# Revit family: LAMP_FIL 45 1400MM OPAL SUSPENDED
name_source: partatom
category: Luminarias
revit_build: Autodesk Revit 2018 (Build: 20170223_1515(x64)
units: mm (PartAtom-declared; Revit-internal decimal feet)

## family parameters
Anfitrión = Cara
Compartido = No
Corte con vacíos al cargar = No
Cota de conector redondo = Diámetro de uso
Origen de luz = Sí
Punto de cálculo de habitación = No
Tipo de pieza = Normal

## types (24) — shared parameters
CRI = 80
Cambio de temperatura de color de luz atenuada = <Ninguno>
Dimensions = 1400x45x80
Elevación por defecto = 1219 mm
Fabricante = LAMP
Filtro de color = 16777215
Gear = Electronic
IEE = A+
Installation instructions = https://www.lamp.es
Insulation class = I
Lamp = MID-POWER LED
Last update = 15/03/2021
MacAdam = 3
Manufacturer URL = http://www.lamp.es
Manufacturer country = Spain
Manufacturer name = LAMP
Material difusor = LAMP_PC Difusor Opal Fil
Material suspension = LAMP_Acero genérico
Power Supply = 220-240V 50/60Hz
Product URL = https://www.lamp.es
Product datasheet = http://www.lamp.es
Protection rating = IP20 / IK07
Type = MID POWER TRIDONIC
Ángulo de inclinación = -90.00°

## per-type parameters (varying)
| type | Archivo de red fotométrica | Descripción | Efficacy | Finish | LED Lifetime | Longitud de línea de emisión | Material perfil | Modelo | Plum | Power | Product code | Weight |
| 3225LM 3000K DALI BLACK | F41SF140MOOP830nb.IES | FIL45 SUR 1400 3250 WW OPAL DALI BK. | 107 lm/W | Matte black RAL 9011 | 70.000 L80 B10 | 610 mm | LAMP_Aluminio Perfil Fil NG | F41SF140MOOP830DB | 20 W | 19 W | F41SF140MOOP830DB | 3.17 kg |
| 3225LM 3000K DALI GREY | F41SF140MOOP830nG.IES | FIL45 SUR 1400 3250 WW OPAL DALI GR. | 107 lm/W | Gloss grey | 70.000 L80 B10 | 610 mm | LAMP_Aluminio Perfil Fil GR | F41SF140MOOP830DG | 20 W | 19 W | F41SF140MOOP830DG | 3.17 kg |
| 3225LM 3000K DALI WHITE | F41SF140MOOP830nW.IES | FIL45 SUR 1400 3250 WW OPAL DALI WH. | 107 lm/W | Matte white RAL 9010 | 70.000 L80 B10 | 610 mm | LAMP_Aluminio Perfil Fil BL | F41SF140MOOP830DW | 20 W | 19 W | F41SF140MOOP830DW | 3.17 kg |
| 3225LM 3000K  BLACK | F41SF140MOOP830NB.IES | FIL45 SUR 1400 3250 WW OPAL BK. | 107 lm/W | Matte black RAL 9011 | 70.000 L80 B10 | 1400 mm  [stored 4.59318 ft] | LAMP_Aluminio Perfil Fil NG | F41SF140MOOP830NB | 20 W | 19 W | F41SF140MOOP830NB | 3.00 kg |
| 3225LM 3000K  GREY | F41SF140MOOP830NG.IES | FIL45 SUR 1400 3250 WW OPAL GR. | 107 lm/W | Gloss grey | 70.000 L80 B10 | 610 mm | LAMP_Aluminio Perfil Fil GR | F41SF140MOOP830NG | 20 W | 19 W | F41SF140MOOP830NG | 3.00 kg |
| 3225LM 3000K  WHITE | F41SF140MOOP830NW.IES | FIL45 SUR 1400 3250 WW OPAL WH. | 107 lm/W | Matte white RAL 9010 | 70.000 L80 B10 | 610 mm | LAMP_Aluminio Perfil Fil BL | F41SF140MOOP830NW | 20 W | 19 W | F41SF140MOOP830NW | 3.00 kg |
| 3225LM 4000K DALI BLACK | F41SF140MOOP840nB.IES | FIL45 SUR 1400 3250 NW OPAL DALI BK. | 117 lm/W | Matte black RAL 9011 | 70.000 L80 B10 | 610 mm | LAMP_Aluminio Perfil Fil NG | F41SF140MOOP840DB | 20 W | 19 W | F41SF140MOOP840DB | 3.17 kg |
| 3225LM 4000K DALI GREY | F41SF140MOOP840nG.IES | FIL45 SUR 1400 3250 NW OPAL DALI GR. | 117 lm/W | Gloss grey | 70.000 L80 B10 | 610 mm | LAMP_Aluminio Perfil Fil GR | F41SF140MOOP840DG | 20 W | 19 W | F41SF140MOOP840DG | 3.17 kg |
| 3225LM 4000K DALI WHITE | F41SF140MOOP840nW.IES | FIL45 SUR 1400 3250 NW OPAL DALI WH. | 117 lm/W | Matte white RAL 9010 | 70.000 L80 B10 | 610 mm | LAMP_Aluminio Perfil Fil BL | F41SF140MOOP840DW | 20 W | 19 W | F41SF140MOOP840DW | 3.17 kg |
| 3225LM 4000K  BLACK | F41SF140MOOP840NB.IES | FIL45 SUR 1400 3250 NW OPAL BK. | 117 lm/W | Matte black RAL 9011 | 70.000 L80 B10 | 610 mm | LAMP_Aluminio Perfil Fil NG | F41SF140MOOP840NB | 20 W | 19 W | F41SF140MOOP840NB | 3.00 kg |
| 3225LM 4000K  GREY | F41SF140MOOP840NG.IES | FIL45 SUR 1400 3250 NW OPAL GR. | 117 lm/W | Gloss grey | 70.000 L80 B10 | 610 mm | LAMP_Aluminio Perfil Fil GR | F41SF140MOOP840NG | 20 W | 19 W | F41SF140MOOP840NG | 3.00 kg |
| 3225LM 4000K  WHITE | F41SF140MOOP840NW.IES | FIL45 SUR 1400 3250 NW OPAL WH. | 117 lm/W | Matte white RAL 9010 | 70.000 L80 B10 | 610 mm | LAMP_Aluminio Perfil Fil BL | F41SF140MOOP840NW | 20 W | 19 W | F41SF140MOOP840NW | 3.00 kg |
| 7750LM 3000K DALI BLACK | F41SF140HOOP830nB.IES | FIL45 SUR 1400 7750 WW OPAL DALI BK. | 95 lm/W | Matte black RAL 9011 | 72.000 L80 B10 | 610 mm | LAMP_Aluminio Perfil Fil NG | F41SF140HOOP830DB | 49 W | 45 W | F41SF140HOOP830DB | 3.19 kg |
| 7750LM 3000K DALI GREY | F41SF140HOOP830nG.IES | FIL45 SUR 1400 7750 WW OPAL DALI GR. | 95 lm/W | Gloss grey | 72.000 L80 B10 | 610 mm | LAMP_Aluminio Perfil Fil GR | F41SF140HOOP830DG | 49 W | 45 W | F41SF140HOOP830DG | 3.19 kg |
| 7750LM 3000K DALI WHITE | F41SF140HOOP830nW.IES | FIL45 SUR 1400 7750 WW OPAL DALI WH. | 95 lm/W | Matte white RAL 9010 | 72.000 L80 B10 | 610 mm | LAMP_Aluminio Perfil Fil BL | F41SF140HOOP830DW | 49 W | 45 W | F41SF140HOOP830DW | 3.19 kg |
| 7750LM 3000K  BLACK | F41SF140HOOP830NB.IES | FIL45 SUR 1400 7750 WW OPAL BK. | 95 lm/W | Matte black RAL 9011 | 72.000 L80 B10 | 610 mm | LAMP_Aluminio Perfil Fil NG | F41SF140HOOP830NB | 49 W | 45 W | F41SF140HOOP830NB | 3.05 kg |
| 7750LM 3000K  GREY | F41SF140HOOP830NG.IES | FIL45 SUR 1400 7750 WW OPAL GR. | 95 lm/W | Gloss grey | 72.000 L80 B10 | 610 mm | LAMP_Aluminio Perfil Fil GR | F41SF140HOOP830NG | 49 W | 45 W | F41SF140HOOP830NG | 3.05 kg |
| 7750LM 3000K  WHITE | F41SF140HOOP830NW.IES | FIL45 SUR 1400 7750 WW OPAL WH. | 95 lm/W | Matte white RAL 9010 | 72.000 L80 B10 | 610 mm | LAMP_Aluminio Perfil Fil BL | F41SF140HOOP830NW | 49 W | 45 W | F41SF140HOOP830NW | 3.05 kg |
| 7750LM 4000K DALI BLACK | F41SF140HOOP840nB.IES | FIL45 SUR 1400 7750 NW OPAL DALI BK. | 95 lm/W | Matte black RAL 9011 | 72.000 L80 B10 | 610 mm | LAMP_Aluminio Perfil Fil NG | F41SF140HOOP840DB | 49 W | 45 W | F41SF140HOOP840DB | 3.19 kg |
| 7750LM 4000K DALI GREY | F41SF140HOOP840nG.IES | FIL45 SUR 1400 7750 NW OPAL DALI GR. | 95 lm/W | Gloss grey | 72.000 L80 B10 | 610 mm | LAMP_Aluminio Perfil Fil GR | F41SF140HOOP840DG | 49 W | 45 W | F41SF140HOOP840DG | 3.19 kg |
| 7750LM 4000K DALI WHITE | F41SF140HOOP840nW.IES | FIL45 SUR 1400 7750 NW OPAL DALI WH. | 95 lm/W | Matte white RAL 9010 | 72.000 L80 B10 | 610 mm | LAMP_Aluminio Perfil Fil BL | F41SF140HOOP840DW | 49 W | 45 W | F41SF140HOOP840DW | 3.19 kg |
| 7750LM 4000K  BLACK | F41SF140HOOP840NB.IES | FIL45 SUR 1400 7750 NW OPAL BK. | 95 lm/W | Matte black RAL 9011 | 72.000 L80 B10 | 610 mm | LAMP_Aluminio Perfil Fil NG | F41SF140HOOP840NB | 49 W | 45 W | F41SF140HOOP840NB | 3.05 kg |
| 7750LM 4000K  GREY | F41SF140HOOP840NG.IES | FIL45 SUR 1400 7750 NW OPAL GR. | 95 lm/W | Gloss grey | 72.000 L80 B10 | 610 mm | LAMP_Aluminio Perfil Fil GR | F41SF140HOOP840NG | 49 W | 45 W | F41SF140HOOP840NG | 3.05 kg |
| 7750LM 4000K  WHITE | F41SF140HOOP840NW.IES | FIL45 SUR 1400 7750 NW OPAL WH. | 95 lm/W | Matte white RAL 9010 | 72.000 L80 B10 | 610 mm | LAMP_Aluminio Perfil Fil BL | F41SF140HOOP840NW | 49 W | 45 W | F41SF140HOOP840NW | 3.05 kg |

note: [stored X ft] marks values corroborated as IEEE doubles in the binary element streams (Revit-internal decimal feet)
